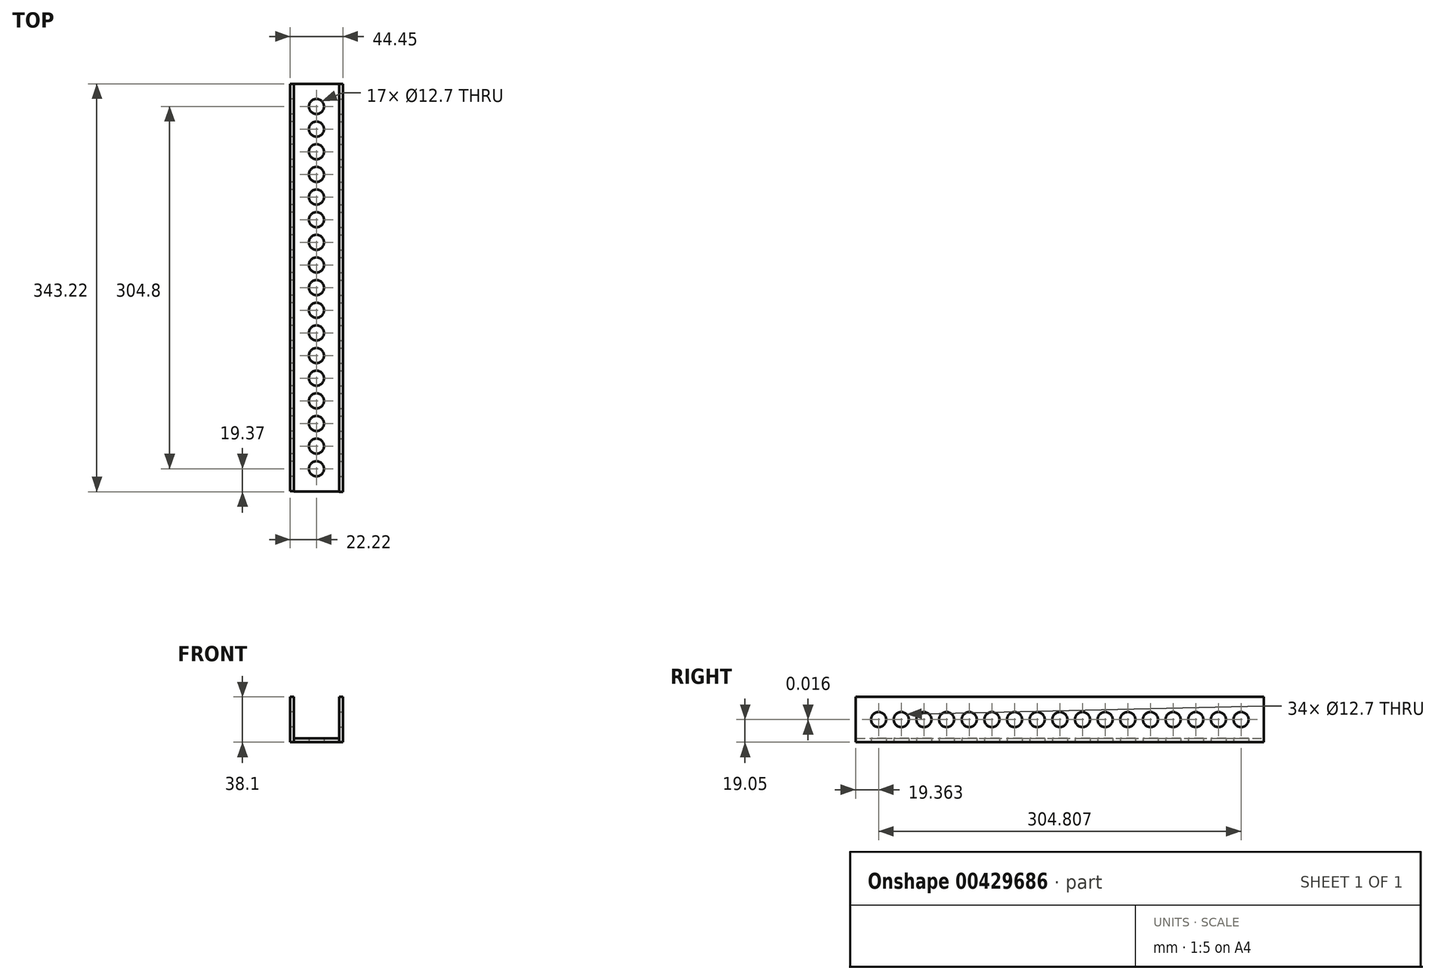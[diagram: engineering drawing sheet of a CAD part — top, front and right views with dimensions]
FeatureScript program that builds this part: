
annotation { "Feature Type Name" : "Feature", "Feature Type Description" : "" }
export const myFeature = defineFeature(function(context is Context, id is Id, definition is map)
    precondition{}
    {
        {
            var Q0;
            Q0=qCreatedBy(makeId("Top.planeOp"),FACE);
            var sketch = newSketch(context, id + "F0", { "sketchPlane" : qUnion([Q0])});
            skLineSegment(sketch, "E0.bottom", {"start": v(-89.28, 285.75) * mm, "end": v(-51.18, 285.75) * mm});
            skLineSegment(sketch, "E0.top", {"start": v(-89.28, -57.15) * mm, "end": v(-51.18, -57.15) * mm});
            skLineSegment(sketch, "E0.left", {"start": v(-89.28, 285.75) * mm, "end": v(-89.28, -57.15) * mm});
            skLineSegment(sketch, "E0.right", {"start": v(-51.18, 285.75) * mm, "end": v(-51.18, -57.15) * mm});
            skCircle(sketch, "E1", {"center": v(-70.23, 266.7) * mm, "radius": 6.35 * mm});
            skCircle(sketch, "E2", {"center": v(-70.23, 247.65) * mm, "radius": 6.35 * mm});
            skCircle(sketch, "E3", {"center": v(-70.23, 228.6) * mm, "radius": 6.35 * mm});
            skCircle(sketch, "E4", {"center": v(-70.23, 209.55) * mm, "radius": 6.35 * mm});
            skCircle(sketch, "E5", {"center": v(-70.23, 152.4) * mm, "radius": 6.35 * mm});
            skCircle(sketch, "E6", {"center": v(-70.23, 171.45) * mm, "radius": 6.35 * mm});
            skCircle(sketch, "E7", {"center": v(-70.23, 190.5) * mm, "radius": 6.35 * mm});
            skPoint(sketch, "E8", {"position": v(-89.28, 114.3) * mm});
            skCircle(sketch, "E9", {"center": v(-70.23, 95.25) * mm, "radius": 6.35 * mm});
            skCircle(sketch, "E10", {"center": v(-70.23, 76.2) * mm, "radius": 6.35 * mm});
            skCircle(sketch, "E11", {"center": v(-70.23, 114.3) * mm, "radius": 6.35 * mm});
            skCircle(sketch, "E12", {"center": v(-70.23, 57.15) * mm, "radius": 6.35 * mm});
            skCircle(sketch, "E13", {"center": v(-70.23, 0) * mm, "radius": 6.35 * mm});
            skCircle(sketch, "E14", {"center": v(-70.23, 38.1) * mm, "radius": 6.35 * mm});
            skCircle(sketch, "E15", {"center": v(-70.23, 19.05) * mm, "radius": 6.35 * mm});
            skCircle(sketch, "E16", {"center": v(-70.23, -38.1) * mm, "radius": 6.35 * mm});
            skCircle(sketch, "E17", {"center": v(-70.23, -19.05) * mm, "radius": 6.35 * mm});
            skPoint(sketch, "E18", {"position": v(-70.23, 285.75) * mm});
            skPoint(sketch, "E19", {"position": v(-70.23, -57.15) * mm});
            skLineSegment(sketch, "E20", {"start": v(-70.23, 285.75) * mm, "end": v(-70.23, -57.15) * mm});
            skLineSegment(sketch, "E21", {"start": v(-70.23, 266.7) * mm, "end": v(-70.23, 247.65) * mm});
            skLineSegment(sketch, "E22", {"start": v(-70.23, 247.65) * mm, "end": v(-70.23, 228.6) * mm});
            skLineSegment(sketch, "E23.bottom", {"start": v(-89.28, 285.75) * mm, "end": v(-92.45, 285.75) * mm});
            skLineSegment(sketch, "E23.top", {"start": v(-89.28, -57) * mm, "end": v(-92.45, -57) * mm});
            skLineSegment(sketch, "E23.left", {"start": v(-89.28, 285.75) * mm, "end": v(-89.28, -57) * mm});
            skLineSegment(sketch, "E23.right", {"start": v(-92.45, 285.75) * mm, "end": v(-92.45, -57) * mm});
            skCircle(sketch, "E24", {"center": v(-70.23, 133.35) * mm, "radius": 6.35 * mm});
            skLineSegment(sketch, "E25.bottom", {"start": v(-51.18, 285.75) * mm, "end": v(-48, 285.75) * mm});
            skLineSegment(sketch, "E25.top", {"start": v(-51.18, -57.47) * mm, "end": v(-48, -57.47) * mm});
            skLineSegment(sketch, "E25.left", {"start": v(-51.18, 285.75) * mm, "end": v(-51.18, -57.47) * mm});
            skLineSegment(sketch, "E25.right", {"start": v(-48, 285.75) * mm, "end": v(-48, -57.47) * mm});
            skSolve(sketch);
        }
        {
            var Q0;
            Q0=qSketchRegion(id+"F0",true);
            extrude(context, id + "F1", {"entities" : qUnion([Q0]), "depth" : 3.17 * mm});
        }
        {
            var Q0;
            Q0=makeQuery(id+"F0.imprint","IMPRINT",FACE,{"disambiguationData":[TD([[makeQuery(id+"F0.imprint","IMPRINT",EDGE,{"derivedFrom":sQuery(id+"F0.wireOp",EDGE,"E23.bottom")}),1.0]])]});
            extrude(context, id + "F2", {"entities" : qUnion([Q0]), "operationType" : NewBodyOperationType.ADD, "depth" : 38.1 * mm});
        }
        {
            var Q0;
            {var subQ0=sQuery(id+"F0.wireOp",EDGE,"E23.right");Q0=makeQuery(id+"F2.boolean.opBoolean","MERGE",FACE,{"derivedFrom":[makeQuery(id+"F1.opExtrude","SWEPT_FACE",FACE,{"disambiguationData":[OSD([subQ0])]}),makeQuery(id+"F2.opExtrude","SWEPT_FACE",FACE,{"disambiguationData":[OSD([subQ0])]})]});}
            var sketch = newSketch(context, id + "F3", { "sketchPlane" : qUnion([Q0])});
            skCircle(sketch, "E26", {"center": v(-266.7, 19.05) * mm, "radius": 6.35 * mm});
            skPoint(sketch, "E27", {"position": v(-285.75, 19.05) * mm});
            skPoint(sketch, "E28", {"position": v(57, 19.05) * mm});
            skLineSegment(sketch, "E29", {"start": v(-285.75, 19.05) * mm, "end": v(57, 19.05) * mm});
            skCircle(sketch, "E30", {"center": v(-247.65, 19.05) * mm, "radius": 6.35 * mm});
            skCircle(sketch, "E31", {"center": v(-228.6, 19.05) * mm, "radius": 6.35 * mm});
            skCircle(sketch, "E32", {"center": v(-209.55, 19.05) * mm, "radius": 6.35 * mm});
            skCircle(sketch, "E33", {"center": v(-190.5, 19.05) * mm, "radius": 6.35 * mm});
            skCircle(sketch, "E34", {"center": v(-171.45, 19.05) * mm, "radius": 6.35 * mm});
            skCircle(sketch, "E35", {"center": v(-152.4, 19.05) * mm, "radius": 6.35 * mm});
            skCircle(sketch, "E36", {"center": v(0, 19.05) * mm, "radius": 6.35 * mm});
            skCircle(sketch, "E37", {"center": v(-19.05, 19.05) * mm, "radius": 6.35 * mm});
            skCircle(sketch, "E38", {"center": v(19.05, 19.07) * mm, "radius": 6.35 * mm});
            skCircle(sketch, "E39", {"center": v(-38.1, 19.05) * mm, "radius": 6.35 * mm});
            skCircle(sketch, "E40", {"center": v(-133.35, 19.05) * mm, "radius": 6.35 * mm});
            skCircle(sketch, "E41", {"center": v(-95.25, 19.05) * mm, "radius": 6.35 * mm});
            skCircle(sketch, "E42", {"center": v(38.1, 19.05) * mm, "radius": 6.35 * mm});
            skCircle(sketch, "E43", {"center": v(-76.2, 19.05) * mm, "radius": 6.35 * mm});
            skCircle(sketch, "E44", {"center": v(-114.3, 19.05) * mm, "radius": 6.35 * mm});
            skCircle(sketch, "E45", {"center": v(-57.15, 19.05) * mm, "radius": 6.35 * mm});
            skSolve(sketch);
        }
        {
            var Q0;
            Q0=qSketchRegion(id+"F3",true);
            extrude(context, id + "F4", {"entities" : qUnion([Q0]), "operationType" : NewBodyOperationType.REMOVE, "oppositeDirection" : true, "depth" : 12.7 * mm});
        }
        {
            var Q0;
            {var subQ3=sQuery(id+"F0.wireOp",EDGE,"E25.bottom");Q0=makeQuery(id+"F0.imprint","IMPRINT",FACE,{"disambiguationData":[TD([[makeQuery(id+"F0.imprint","IMPRINT",EDGE,{"derivedFrom":subQ3}),-1.0]])]});}
            extrude(context, id + "F5", {"entities" : qUnion([Q0]), "operationType" : NewBodyOperationType.ADD, "depth" : 38.1 * mm});
        }
        {
            var Q0;
            {var subQ0=sQuery(id+"F0.wireOp",EDGE,"E25.right");Q0=makeQuery(id+"F5.boolean.opBoolean","MERGE",FACE,{"derivedFrom":[makeQuery(id+"F1.opExtrude","SWEPT_FACE",FACE,{"disambiguationData":[OSD([subQ0])]}),makeQuery(id+"F5.opExtrude","SWEPT_FACE",FACE,{"disambiguationData":[OSD([subQ0])]})]});}
            var sketch = newSketch(context, id + "F6", { "sketchPlane" : qUnion([Q0])});
            skCircle(sketch, "E46", {"center": v(266.7, 19.05) * mm, "radius": 6.35 * mm});
            skPoint(sketch, "E47", {"position": v(285.75, 19.05) * mm});
            skPoint(sketch, "E48", {"position": v(-57.47, 19.05) * mm});
            skLineSegment(sketch, "E49", {"start": v(285.75, 19.05) * mm, "end": v(-57.47, 19.05) * mm});
            skCircle(sketch, "E50", {"center": v(247.65, 19.05) * mm, "radius": 6.35 * mm});
            skCircle(sketch, "E51", {"center": v(209.54, 19.05) * mm, "radius": 6.35 * mm});
            skCircle(sketch, "E52", {"center": v(190.5, 19.05) * mm, "radius": 6.35 * mm});
            skCircle(sketch, "E53", {"center": v(152.4, 19.05) * mm, "radius": 6.35 * mm});
            skCircle(sketch, "E54", {"center": v(133.34, 19.05) * mm, "radius": 6.35 * mm});
            skCircle(sketch, "E55", {"center": v(114.3, 19.05) * mm, "radius": 6.35 * mm});
            skCircle(sketch, "E56", {"center": v(95.24, 19.05) * mm, "radius": 6.35 * mm});
            skCircle(sketch, "E57", {"center": v(76.2, 19.05) * mm, "radius": 6.35 * mm});
            skCircle(sketch, "E58", {"center": v(57.14, 19.05) * mm, "radius": 6.35 * mm});
            skCircle(sketch, "E59", {"center": v(19.04, 19.05) * mm, "radius": 6.35 * mm});
            skCircle(sketch, "E60", {"center": v(0, 19.05) * mm, "radius": 6.35 * mm});
            skCircle(sketch, "E61", {"center": v(38.1, 19.05) * mm, "radius": 6.35 * mm});
            skCircle(sketch, "E62", {"center": v(228.6, 19.05) * mm, "radius": 6.35 * mm});
            skCircle(sketch, "E63", {"center": v(171.44, 19.05) * mm, "radius": 6.35 * mm});
            skCircle(sketch, "E64", {"center": v(-19.06, 19.05) * mm, "radius": 6.35 * mm});
            skCircle(sketch, "E65", {"center": v(-38.1, 19.05) * mm, "radius": 6.35 * mm});
            skSolve(sketch);
        }
        {
            var Q0;
            Q0=qSketchRegion(id+"F6",true);
            extrude(context, id + "F7", {"entities" : qUnion([Q0]), "operationType" : NewBodyOperationType.REMOVE, "oppositeDirection" : true, "depth" : 12.7 * mm});
        }
    });
